# Revit family: SKC08R
name_source: partatom
category: Lighting Fixtures
units: mm (PartAtom-declared; Revit-internal decimal feet)

## family parameters
Cut with Voids When Loaded = Yes
Host = Face
Light Source = Yes
Maintain Annotation Orientation = No
Part Type = Normal
Room Calculation Point = No
Round Connector Dimension = Use Diameter
Shared = No

## types (16) — shared parameters
Color Filter = 16777215
Default Elevation = 0' - 0"
Dimming Lamp Color Temperature Shift = <None>
Input Voltage = 120-277V
Lamp = LED
Load Classification = Lighting
Manufacturer = Above All Lighting
Power Factor = 0.9
R = 0' - 4"
Tilt Angle = 90.00°
Trim = 0' - 0 11/16"
URL = https://www.abovealllighting.com
r = 0' - 3"

## per-type parameters (varying)
| type | CRI | Model | Photometric Web File | Wattage Comments |
| SKC08R-08LM-2700K-CRI90 | 90 | SKC08R-08LM-27901 | SKC08R-08LM27901(G).IES | 9.5W |
| SKC08R-08LM-3000K-CRI90 | 90 | SKC08R-08LM-30901 | SKC08R-08LM30901(G).IES | 9.5W |
| SKC08R-08LM-3500K-CRI90 | 90 | SKC08R-08LM-35901 | SKC08R-08LM35901(G).IES | 9.5W |
| SKC08R-08LM-4000K-CRI90 | 90 | SKC08R-08LM-40901 | SKC08R-08LM40901(G).IES | 9.5W |
| SKC08R-10LM-2700K-CRI90 | 90 | SKC08R-10LM-27901 | SKC08R-10LM27901(G).IES | 13W |
| SKC08R-10LM-3000K-CRI90 | 90 | SKC08R-10LM-30901 | SKC08R-10LM30901(G).IES | 13W |
| SKC08R-10LM-3500K-CRI90 | 90 | SKC08R-10LM-35901 | SKC08R-10LM35901(G).IES | 13W |
| SKC08R-10LM-4000K-CRI90 | 90 | SKC08R-10LM-40901 | SKC08R-10LM40901(G).IES | 13W |
| SKC08R-08LM-2700K-CRI80 | 80 | SKC08R-08LM-27801 | SKC08R-08LM27801(G).IES | 9.5W |
| SKC08R-08LM-3000K-CRI80 | 80 | SKC08R-08LM-30801 | SKC08R-08LM30801(G).IES | 9.5W |
| SKC08R-08LM-3500K-CRI80 | 80 | SKC08R-08LM-35801 | SKC08R-08LM35801(G).IES | 9.5W |
| SKC08R-08LM-4000K-CRI80 | 80 | SKC08R-08LM-40801 | SKC08R-08LM40801(G).IES | 9.5W |
| SKC08R-10LM-2700K-CRI80 | 90 | SKC08R-10LM-27801 | SKC08R-10LM27801(G).IES | 13W |
| SKC08R-10LM-3000K-CRI80 | 90 | SKC08R-10LM-30801 | SKC08R-10LM30801(G).IES | 13W |
| SKC08R-10LM-3500K-CRI80 | 90 | SKC08R-10LM-35801 | SKC08R-10LM35801(G).IES | 13W |
| SKC08R-10LM-4000K-CRI80 | 90 | SKC08R-10LM-40801 | SKC08R-10LM40801(G).IES | 13W |

## geometry (parser evidence)
native form markers: Sweep x3
no freeform markers — native parametric forms only
